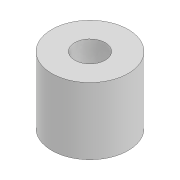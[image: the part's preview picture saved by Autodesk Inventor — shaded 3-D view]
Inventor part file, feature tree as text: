
AUTODESK INVENTOR PART (.ipt)
format: ipt  version: 2022 (Build 260153000, 153)  size: 83,456 bytes
history: native  units: mm
features: extrude x1, sketch x1
ambient origin geometry x8: Origin, YZ Plane, XZ Plane, XY Plane, X Axis, Y Axis, Z Axis, Center Point
bodies: Solid1 (feature_tree)
feature tree (2):
  extrude  "Extrusion1"  Depth=7.0mm
  sketch  "Sketch1"  dims[d0=3.2mm d1=8.0mm d2=7.0mm d3=0.0mm]
